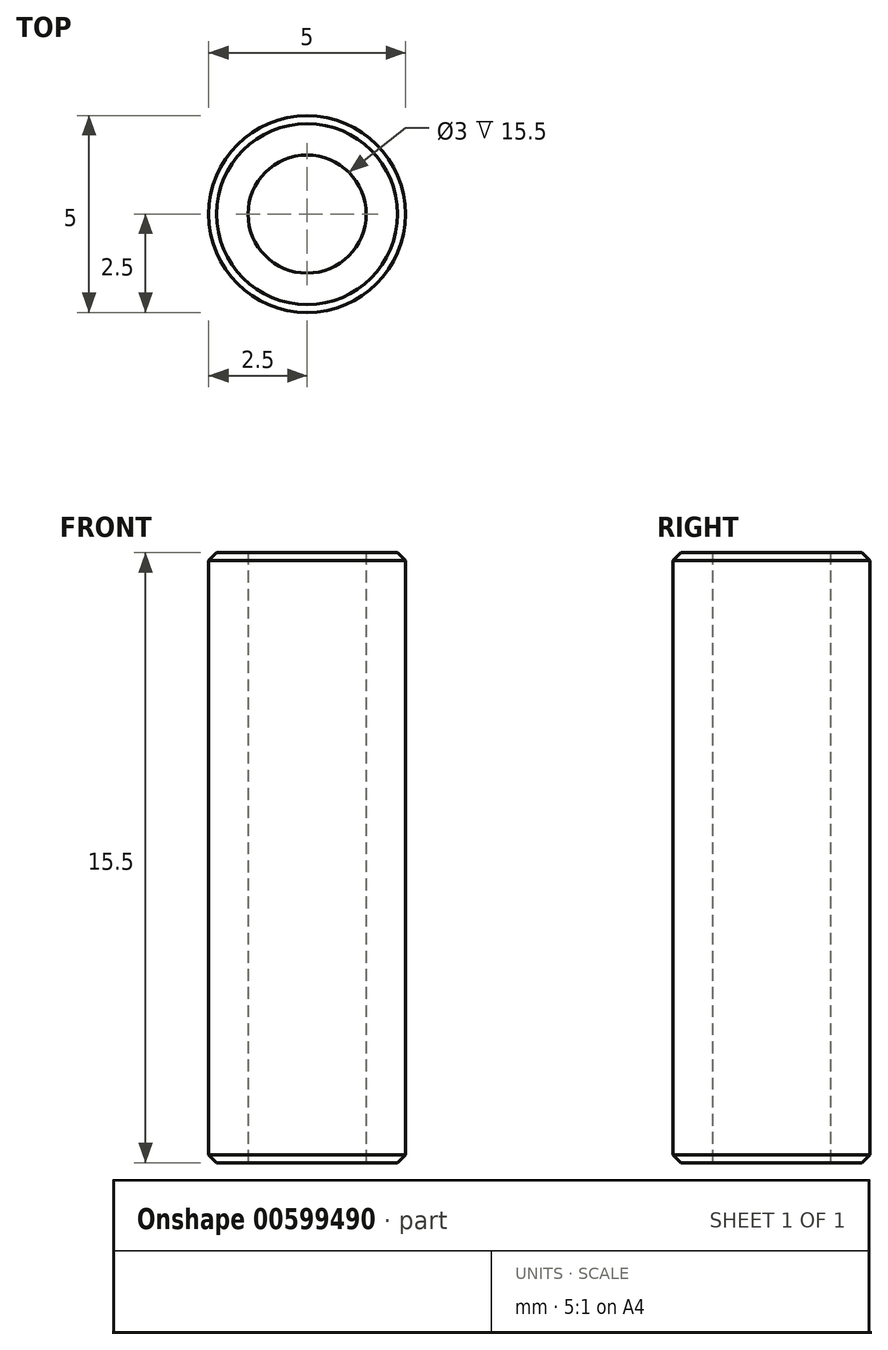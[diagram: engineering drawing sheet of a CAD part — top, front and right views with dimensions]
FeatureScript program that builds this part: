
annotation { "Feature Type Name" : "Feature", "Feature Type Description" : "" }
export const myFeature = defineFeature(function(context is Context, id is Id, definition is map)
    precondition{}
    {
        {
            var Q0;
            Q0=qCreatedBy(makeId("Top.planeOp"),FACE);
            var sketch = newSketch(context, id + "F0", { "sketchPlane" : qUnion([Q0])});
            skCircle(sketch, "E0", {"center": v(0, 0) * mm, "radius": 2.5 * mm});
            skSolve(sketch);
        }
        {
            var Q0;
            Q0=qSketchRegion(id+"F0",true);
            extrude(context, id + "F1", {"entities" : qUnion([Q0]), "depth" : 15.5 * mm, "offsetDistance" : 25 * mm});
        }
        {
            var Q0;
            Q0=makeQuery(id+"F1.opExtrude","CAP_FACE",FACE,{"disambiguationData":[OSD([sQuery(id+"F0.wireOp",EDGE,"E0")])],"isStart":false});
            var Q1;
            Q1=makeQuery(id+"F1.opExtrude","CAP_FACE",FACE,{"disambiguationData":[OSD([sQuery(id+"F0.wireOp",EDGE,"E0")])],"isStart":true});
            chamfer(context, id + "F2", {"entities" : qUnion([Q0, Q1]), "width" : 0.2 * mm, "tangentPropagation" : true});
        }
        {
            var Q0;
            Q0=sQuery(id+"F0.wireOp",VERTEX,"E0.center");
            var Q1;
            Q1=makeQuery(id+"F1.opExtrude","SWEPT_BODY",BODY,{"disambiguationData":[OSD([sQuery(id+"F0.wireOp",EDGE,"E0")])]});
            hole(context, id + "F3", {"style" : HoleStyle.SIMPLE, "endStyle" : HoleEndStyle.THROUGH, "oppositeDirection" : true, "holeDiameter" : 3 * mm, "isTappedThrough" : true, "tappedDepth" : 12 * mm, "tapClearance" : 3, "startFromSketch" : true, "locations" : qUnion([Q0]), "scope" : qUnion([Q1])});
        }
    });
